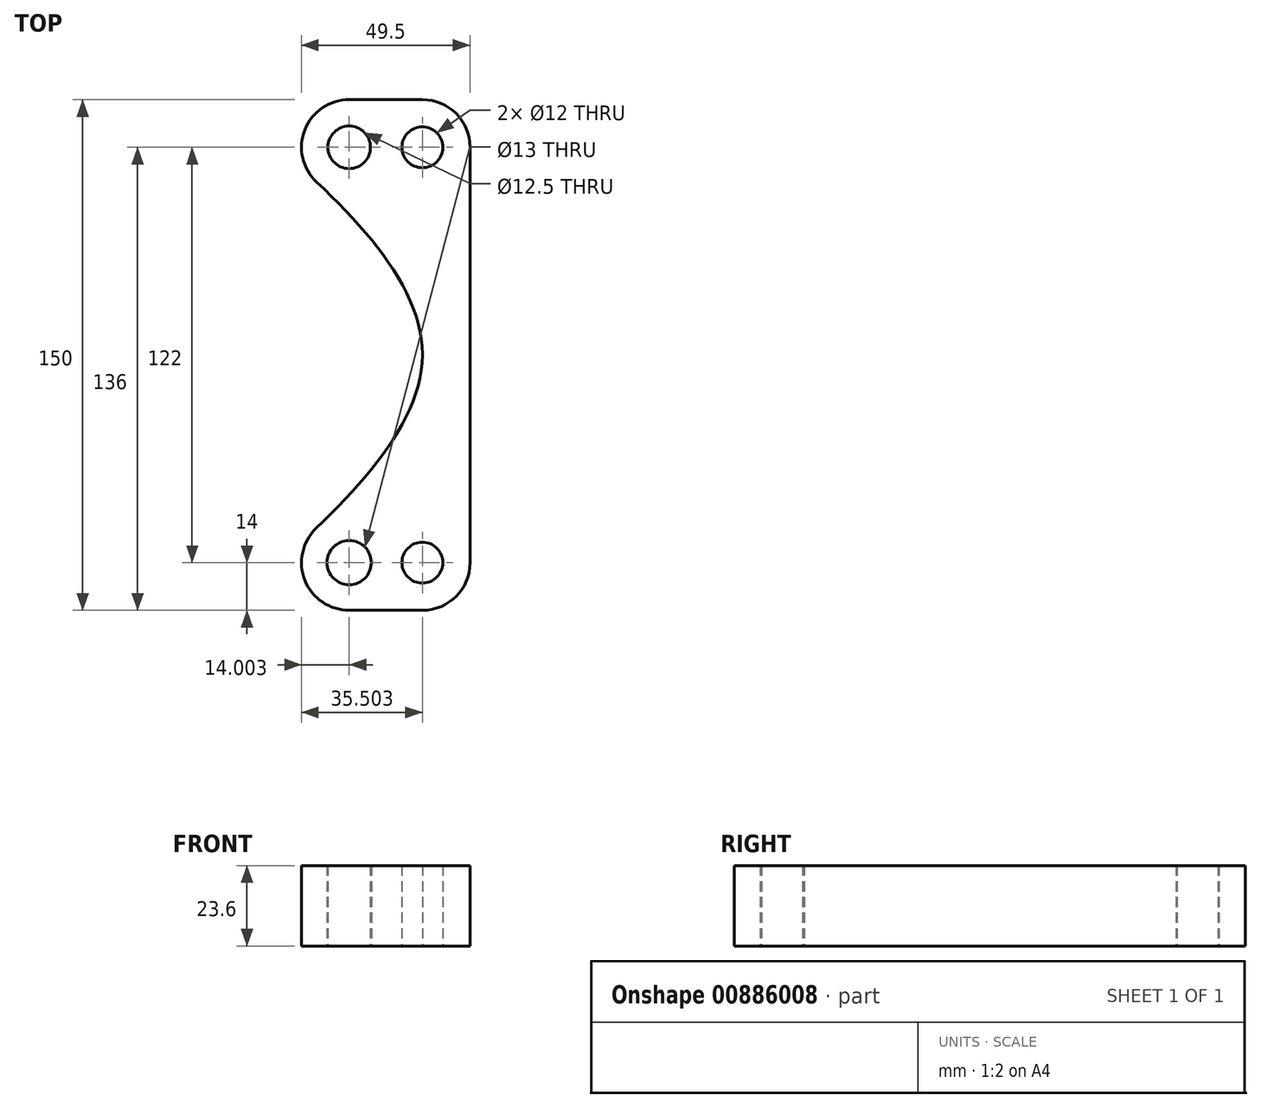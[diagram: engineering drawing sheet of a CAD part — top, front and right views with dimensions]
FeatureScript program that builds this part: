
annotation { "Feature Type Name" : "Feature", "Feature Type Description" : "" }
export const myFeature = defineFeature(function(context is Context, id is Id, definition is map)
    precondition{}
    {
        {
            var Q0;
            Q0=qCreatedBy(makeId("Top.planeOp"),FACE);
            var sketch = newSketch(context, id + "F0", { "sketchPlane" : qUnion([Q0])});
            skCircle(sketch, "E0", {"center": v(0, 0) * mm, "radius": 169 * mm, "construction": true});
            skCircle(sketch, "E1", {"center": v(0, 0) * mm, "radius": 70 * mm, "construction": true});
            skCircle(sketch, "E2", {"center": v(-34.34, 61) * mm, "radius": 6 * mm});
            skCircle(sketch, "E3", {"center": v(-34.34, -61) * mm, "radius": 6 * mm});
            skLineSegment(sketch, "E4", {"start": v(-34.34, -61) * mm, "end": v(-34.34, 61) * mm});
            skLineSegment(sketch, "E5", {"start": v(-169, 0) * mm, "end": v(-122, 0) * mm});
            skLineSegment(sketch, "E6", {"start": v(-70, 0) * mm, "end": v(-122, 0) * mm});
            skCircle(sketch, "E7", {"center": v(-55.84, 61) * mm, "radius": 6.25 * mm});
            skCircle(sketch, "E8", {"center": v(-55.84, -61) * mm, "radius": 6.5 * mm});
            skLineSegment(sketch, "E9", {"start": v(-34.34, -61) * mm, "end": v(-55.84, -61) * mm});
            skLineSegment(sketch, "E10", {"start": v(-34.34, 61) * mm, "end": v(-55.84, 61) * mm});
            skLineSegment(sketch, "E11", {"start": v(-55.84, -61) * mm, "end": v(-55.84, 61) * mm, "construction": true});
            skCircle(sketch, "E12", {"center": v(-34.34, 61) * mm, "radius": 14 * mm});
            skCircle(sketch, "E13", {"center": v(-34.34, -61) * mm, "radius": 14 * mm});
            skCircle(sketch, "E14", {"center": v(-55.84, -61) * mm, "radius": 14 * mm});
            skCircle(sketch, "E15", {"center": v(-55.84, 61) * mm, "radius": 14 * mm});
            skLineSegment(sketch, "E16", {"start": v(-55.84, 75) * mm, "end": v(-34.34, 75) * mm});
            skLineSegment(sketch, "E17", {"start": v(-55.84, -75) * mm, "end": v(-34.34, -75) * mm});
            skLineSegment(sketch, "E18", {"start": v(-20.34, 61) * mm, "end": v(-20.34, -61) * mm});
            skFitSpline(sketch, "E19", {"points": [v(-72, 56.71) * mm, v(-34.34, 0) * mm, v(-72, -56.95) * mm], "startDerivative": vector(119.1, -104.05) * mm, "endDerivative": vector(-117.01, -107.15) * mm});
            skSolve(sketch);
        }
        {
            var Q0;
            Q0=qSketchRegion(id+"F0",true);
            var Q1;
            {var subQ5=sQuery(id+"F0.wireOp",EDGE,"E10");var subQ6=sQuery(id+"F0.wireOp",EDGE,"E2");var subQ7=makeQuery(id+"F0.imprint","INTERSECT",VERTEX,{"derivedFrom":[subQ6,subQ5]});Q1=makeQuery(id+"F0.imprint","IMPRINT",FACE,{"disambiguationData":[TD([[makeQuery(id+"F0.imprint","IMPRINT",EDGE,{"disambiguationData":[TD([[subQ7,1.0]])],"derivedFrom":subQ6}),-1.0]])]});}
            var Q2;
            {var subQ5=sQuery(id+"F0.wireOp",EDGE,"E10");var subQ6=sQuery(id+"F0.wireOp",EDGE,"E2");var subQ7=makeQuery(id+"F0.imprint","INTERSECT",VERTEX,{"derivedFrom":[subQ6,subQ5]});Q2=makeQuery(id+"F0.imprint","IMPRINT",FACE,{"disambiguationData":[TD([[makeQuery(id+"F0.imprint","IMPRINT",EDGE,{"disambiguationData":[TD([[subQ7,-1.0]])],"derivedFrom":subQ6}),-1.0]])]});}
            var Q3;
            {var subQ0=sQuery(id+"F0.wireOp",EDGE,"E15");var subQ1=sQuery(id+"F0.wireOp",EDGE,"E2");var subQ2=makeQuery(id+"F0.imprint","INTERSECT",VERTEX,{"disambiguationData":[OD(1.0)],"derivedFrom":[subQ1,subQ0]});Q3=makeQuery(id+"F0.imprint","IMPRINT",FACE,{"disambiguationData":[TD([[makeQuery(id+"F0.imprint","IMPRINT",EDGE,{"disambiguationData":[TD([[subQ2,-1.0]])],"derivedFrom":subQ1}),-1.0]])]});}
            var Q4;
            {var subQ0=sQuery(id+"F0.wireOp",EDGE,"E14");var subQ1=sQuery(id+"F0.wireOp",EDGE,"E3");var subQ2=makeQuery(id+"F0.imprint","INTERSECT",VERTEX,{"disambiguationData":[OD(0.0)],"derivedFrom":[subQ1,subQ0]});Q4=makeQuery(id+"F0.imprint","IMPRINT",FACE,{"disambiguationData":[TD([[makeQuery(id+"F0.imprint","IMPRINT",EDGE,{"disambiguationData":[TD([[subQ2,1.0]])],"derivedFrom":subQ1}),-1.0]])]});}
            var Q5;
            {var subQ3=sQuery(id+"F0.wireOp",EDGE,"E14");var subQ6=sQuery(id+"F0.wireOp",EDGE,"E3");var subQ9=makeQuery(id+"F0.imprint","INTERSECT",VERTEX,{"disambiguationData":[OD(0.0)],"derivedFrom":[subQ6,subQ3]});Q5=makeQuery(id+"F0.imprint","IMPRINT",FACE,{"disambiguationData":[TD([[makeQuery(id+"F0.imprint","IMPRINT",EDGE,{"disambiguationData":[TD([[subQ9,-1.0]])],"derivedFrom":subQ6}),-1.0]])]});}
            var Q6;
            {var subQ5=sQuery(id+"F0.wireOp",EDGE,"E9");var subQ7=sQuery(id+"F0.wireOp",EDGE,"E3");var subQ8=makeQuery(id+"F0.imprint","INTERSECT",VERTEX,{"derivedFrom":[subQ7,subQ5]});Q6=makeQuery(id+"F0.imprint","IMPRINT",FACE,{"disambiguationData":[TD([[makeQuery(id+"F0.imprint","IMPRINT",EDGE,{"disambiguationData":[TD([[subQ8,-1.0]])],"derivedFrom":subQ7}),-1.0]])]});}
            var Q7;
            {var subQ0=sQuery(id+"F0.wireOp",EDGE,"E12");var subQ1=sQuery(id+"F0.wireOp",EDGE,"E10");var subQ2=makeQuery(id+"F0.imprint","INTERSECT",VERTEX,{"derivedFrom":[subQ1,subQ0]});Q7=makeQuery(id+"F0.imprint","IMPRINT",FACE,{"disambiguationData":[TD([[makeQuery(id+"F0.imprint","IMPRINT",EDGE,{"disambiguationData":[TD([[subQ2,1.0]])],"derivedFrom":subQ1}),-1.0]])]});}
            var Q8;
            {var subQ0=sQuery(id+"F0.wireOp",EDGE,"E12");var subQ1=sQuery(id+"F0.wireOp",EDGE,"E10");var subQ2=makeQuery(id+"F0.imprint","INTERSECT",VERTEX,{"derivedFrom":[subQ1,subQ0]});Q8=makeQuery(id+"F0.imprint","IMPRINT",FACE,{"disambiguationData":[TD([[makeQuery(id+"F0.imprint","IMPRINT",EDGE,{"disambiguationData":[TD([[subQ2,1.0]])],"derivedFrom":subQ1}),1.0]])]});}
            var Q9;
            {var subQ1=sQuery(id+"F0.wireOp",EDGE,"E3");var subQ5=sQuery(id+"F0.wireOp",EDGE,"E4");var subQ6=makeQuery(id+"F0.imprint","INTERSECT",VERTEX,{"derivedFrom":[subQ1,subQ5]});Q9=makeQuery(id+"F0.imprint","IMPRINT",FACE,{"disambiguationData":[TD([[makeQuery(id+"F0.imprint","IMPRINT",EDGE,{"disambiguationData":[TD([[subQ6,-1.0]])],"derivedFrom":subQ1}),-1.0]])]});}
            var Q10;
            {var subQ0=sQuery(id+"F0.wireOp",EDGE,"E13");var subQ1=sQuery(id+"F0.wireOp",EDGE,"E9");var subQ2=makeQuery(id+"F0.imprint","INTERSECT",VERTEX,{"derivedFrom":[subQ1,subQ0]});Q10=makeQuery(id+"F0.imprint","IMPRINT",FACE,{"disambiguationData":[TD([[makeQuery(id+"F0.imprint","IMPRINT",EDGE,{"disambiguationData":[TD([[subQ2,1.0]])],"derivedFrom":subQ1}),-1.0]])]});}
            var Q11;
            {var subQ0=sQuery(id+"F0.wireOp",EDGE,"E13");var subQ1=sQuery(id+"F0.wireOp",EDGE,"E9");var subQ2=makeQuery(id+"F0.imprint","INTERSECT",VERTEX,{"derivedFrom":[subQ1,subQ0]});Q11=makeQuery(id+"F0.imprint","IMPRINT",FACE,{"disambiguationData":[TD([[makeQuery(id+"F0.imprint","IMPRINT",EDGE,{"disambiguationData":[TD([[subQ2,1.0]])],"derivedFrom":subQ1}),1.0]])]});}
            extrude(context, id + "F1", {"entities" : qUnion([Q0, Q1, Q2, Q3, Q4, Q5, Q6, Q7, Q8, Q9, Q10, Q11]), "depth" : 23.6 * mm, "offsetDistance" : 25 * mm});
        }
    });
